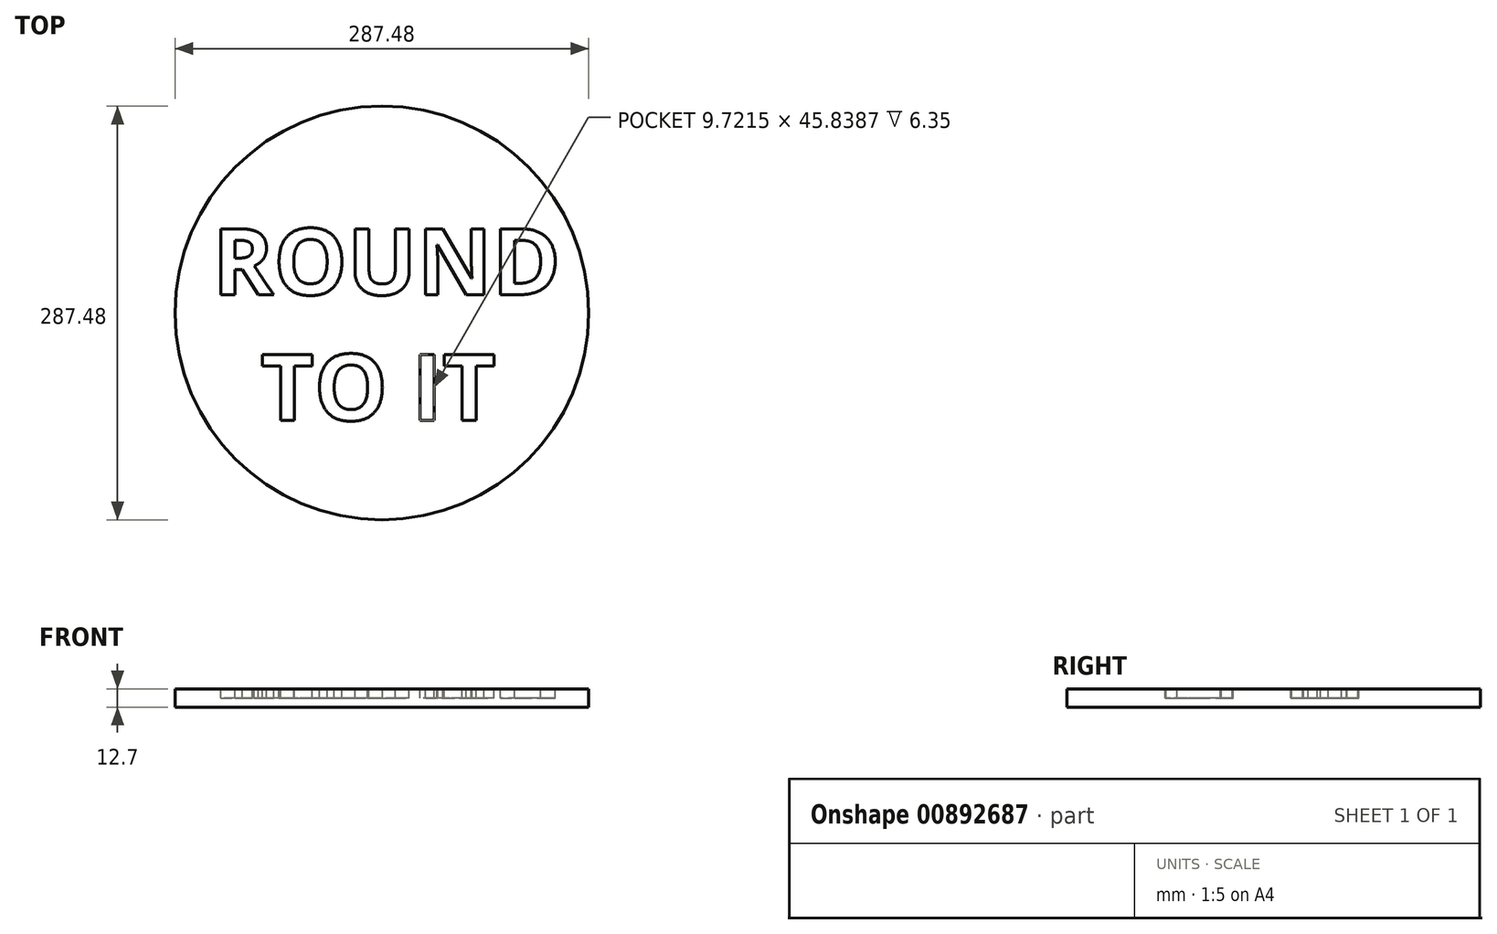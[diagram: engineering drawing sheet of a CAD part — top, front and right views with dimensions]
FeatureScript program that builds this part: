
annotation { "Feature Type Name" : "Feature", "Feature Type Description" : "" }
export const myFeature = defineFeature(function(context is Context, id is Id, definition is map)
    precondition{}
    {
        {
            var Q0;
            Q0=qCreatedBy(makeId("Top.planeOp"),FACE);
            var sketch = newSketch(context, id + "F0", { "sketchPlane" : qUnion([Q0])});
            skCircle(sketch, "E0", {"center": v(0, 0) * mm, "radius": 143.74 * mm});
            skSolve(sketch);
        }
        {
            var Q0;
            Q0 = qSketchRegion(id + "F0", true);
            extrude(context, id + "F1", {"entities" : qUnion([Q0]), "depth" : 12.7 * mm, "offsetDistance" : 25.4 * mm});
        }
        {
            var Q0;
            Q0=makeQuery(id+"F1.opExtrude","CAP_FACE",FACE,{"disambiguationData":[OSD([sQuery(id+"F0.wireOp",EDGE,"E0")])],"isStart":false});
            var sketch = newSketch(context, id + "F2", { "sketchPlane" : qUnion([Q0])});
            skText(sketch, "E1", { "text": "ROUND\n  TO IT", "fontName": "OpenSans-Bold.ttf"});
            const initialGuessF2  = {"E1": [-0.11762, 0.01266, 1, 0, 0.04623]};
            skSetInitialGuess(sketch, initialGuessF2);
            skSolve(sketch);
        }
        {
            var Q0;
            Q0 = qSketchRegion(id + "F2", true);
            extrude(context, id + "F3", {"entities" : qUnion([Q0]), "operationType" : NewBodyOperationType.REMOVE, "oppositeDirection" : true, "depth" : 6.35 * mm, "offsetDistance" : 25.4 * mm});
        }
    });
